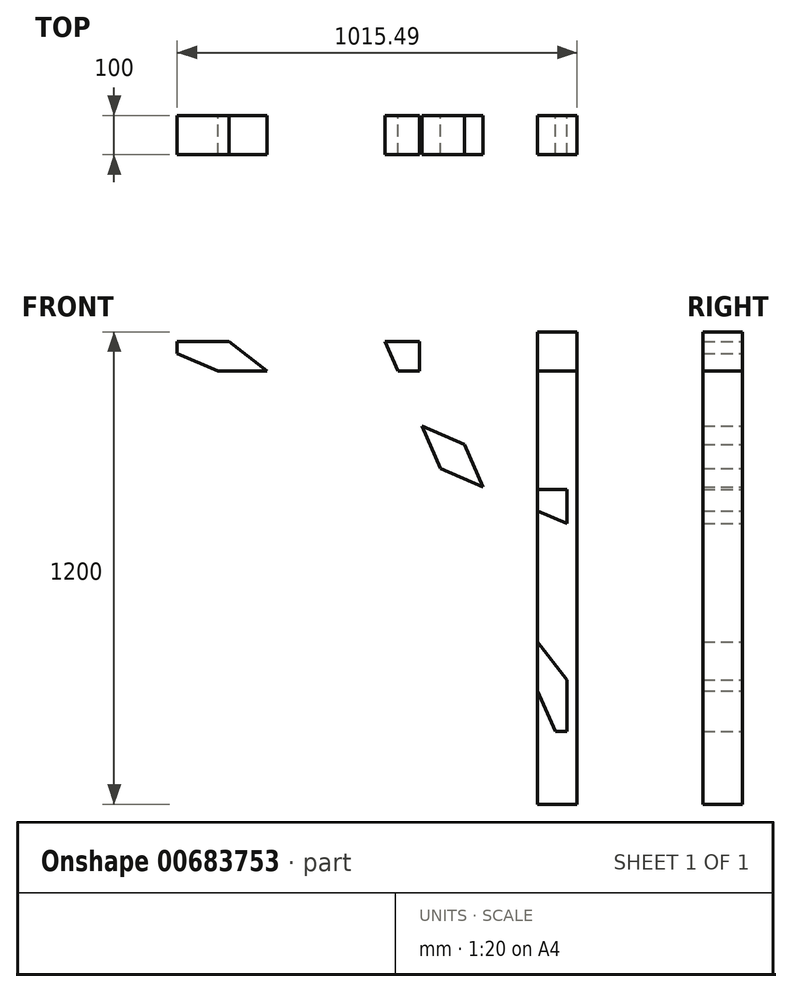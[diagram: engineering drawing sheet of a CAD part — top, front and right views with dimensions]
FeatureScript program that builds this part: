
annotation { "Feature Type Name" : "Feature", "Feature Type Description" : "" }
export const myFeature = defineFeature(function(context is Context, id is Id, definition is map)
    precondition{}
    {
        {
            var Q0;
            Q0=qCreatedBy(makeId("Front.planeOp"),FACE);
            var sketch = newSketch(context, id + "F0", { "sketchPlane" : qUnion([Q0])});
            skLineSegment(sketch, "E0.bottom", {"start": v(0, 1200) * mm, "end": v(1200, 1200) * mm});
            skLineSegment(sketch, "E0.top", {"start": v(0, 1100) * mm, "end": v(1200, 1100) * mm});
            skLineSegment(sketch, "E0.left", {"start": v(0, 1200) * mm, "end": v(0, 1100) * mm});
            skLineSegment(sketch, "E0.right", {"start": v(1200, 1200) * mm, "end": v(1200, 1100) * mm});
            skLineSegment(sketch, "E1.bottom", {"start": v(1200, 1200) * mm, "end": v(1100, 1200) * mm});
            skLineSegment(sketch, "E1.top", {"start": v(1200, 0) * mm, "end": v(1100, 0) * mm});
            skLineSegment(sketch, "E1.left", {"start": v(1200, 1200) * mm, "end": v(1200, 0) * mm});
            skLineSegment(sketch, "E1.right", {"start": v(1100, 1200) * mm, "end": v(1100, 0) * mm});
            skLineSegment(sketch, "E2", {"start": v(1200, 1200) * mm, "end": v(0, 0) * mm, "construction": true});
            skLineSegment(sketch, "E3", {"start": v(0, 1175) * mm, "end": v(1200, 1175) * mm, "construction": true});
            skLineSegment(sketch, "E4", {"start": v(1175, 1200) * mm, "end": v(1175, 0) * mm, "construction": true});
            skLineSegment(sketch, "E5", {"start": v(1145, 1200) * mm, "end": v(1145, 0) * mm, "construction": true});
            skLineSegment(sketch, "E6", {"start": v(0, 1145) * mm, "end": v(1200, 1145) * mm, "construction": true});
            skLineSegment(sketch, "E7", {"start": v(712.71, 1175) * mm, "end": v(1145, 184.5) * mm});
            skLineSegment(sketch, "E8", {"start": v(1145, 184.5) * mm, "end": v(1175, 184.5) * mm});
            skLineSegment(sketch, "E9", {"start": v(1175, 184.5) * mm, "end": v(1175, 315.77) * mm});
            skLineSegment(sketch, "E10", {"start": v(1175, 315.77) * mm, "end": v(1100, 412.61) * mm});
            skLineSegment(sketch, "E11", {"start": v(1100, 412.61) * mm, "end": v(1100, 487.61) * mm});
            skLineSegment(sketch, "E12", {"start": v(1100, 487.61) * mm, "end": v(832.73, 1100) * mm});
            skLineSegment(sketch, "E13", {"start": v(832.73, 1100) * mm, "end": v(800, 1100) * mm});
            skLineSegment(sketch, "E14", {"start": v(800, 1100) * mm, "end": v(800, 1175) * mm});
            skLineSegment(sketch, "E15", {"start": v(800, 1175) * mm, "end": v(712.71, 1175) * mm});
            skLineSegment(sketch, "E16", {"start": v(1175, 712.71) * mm, "end": v(184.5, 1145) * mm});
            skLineSegment(sketch, "E17", {"start": v(184.5, 1145) * mm, "end": v(184.5, 1175) * mm});
            skLineSegment(sketch, "E18", {"start": v(184.5, 1175) * mm, "end": v(315.77, 1175) * mm});
            skLineSegment(sketch, "E19", {"start": v(315.77, 1175) * mm, "end": v(412.61, 1100) * mm});
            skLineSegment(sketch, "E20", {"start": v(412.61, 1100) * mm, "end": v(487.61, 1100) * mm});
            skLineSegment(sketch, "E21", {"start": v(487.61, 1100) * mm, "end": v(1100, 832.73) * mm});
            skPoint(sketch, "E22", {"position": v(913.94, 913.94) * mm});
            skLineSegment(sketch, "E23", {"start": v(1100, 832.73) * mm, "end": v(1100, 800) * mm});
            skLineSegment(sketch, "E24", {"start": v(1100, 800) * mm, "end": v(1175, 800) * mm});
            skLineSegment(sketch, "E25", {"start": v(1175, 800) * mm, "end": v(1175, 712.71) * mm});
            skSolve(sketch);
        }
        {
            var Q0;
            {var subQ0=sQuery(id+"F0.wireOp",EDGE,"E14");Q0=makeQuery(id+"F0.imprint","IMPRINT",FACE,{"disambiguationData":[TD([[makeQuery(id+"F0.imprint","IMPRINT",EDGE,{"derivedFrom":subQ0}),1.0]])]});}
            var Q1;
            {var subQ0=sQuery(id+"F0.wireOp",EDGE,"E13");Q1=makeQuery(id+"F0.imprint","IMPRINT",FACE,{"disambiguationData":[TD([[makeQuery(id+"F0.imprint","IMPRINT",EDGE,{"derivedFrom":subQ0}),1.0]])]});}
            var Q2;
            {var subQ0=sQuery(id+"F0.wireOp",EDGE,"E16");var subQ1=sQuery(id+"F0.wireOp",EDGE,"E7");var subQ2=makeQuery(id+"F0.imprint","INTERSECT",VERTEX,{"derivedFrom":[subQ1,subQ0]});Q2=makeQuery(id+"F0.imprint","IMPRINT",FACE,{"disambiguationData":[TD([[makeQuery(id+"F0.imprint","IMPRINT",EDGE,{"disambiguationData":[TD([[subQ2,1.0]])],"derivedFrom":subQ1}),1.0]])]});}
            var Q3;
            {var subQ1=sQuery(id+"F0.wireOp",EDGE,"E11");Q3=makeQuery(id+"F0.imprint","IMPRINT",FACE,{"disambiguationData":[TD([[makeQuery(id+"F0.imprint","IMPRINT",EDGE,{"derivedFrom":subQ1}),1.0]])]});}
            var Q4;
            {var subQ0=sQuery(id+"F0.wireOp",EDGE,"E8");Q4=makeQuery(id+"F0.imprint","IMPRINT",FACE,{"disambiguationData":[TD([[makeQuery(id+"F0.imprint","IMPRINT",EDGE,{"derivedFrom":subQ0}),1.0]])]});}
            extrude(context, id + "F1", {"entities" : qUnion([Q0, Q1, Q2, Q3, Q4]), "depth" : 100 * mm, "offsetDistance" : 25 * mm});
        }
        {
            var Q0;
            {var subQ0=sQuery(id+"F0.wireOp",EDGE,"E17");Q0=makeQuery(id+"F0.imprint","IMPRINT",FACE,{"disambiguationData":[TD([[makeQuery(id+"F0.imprint","IMPRINT",EDGE,{"derivedFrom":subQ0}),-1.0]])]});}
            var Q1;
            {var subQ0=sQuery(id+"F0.wireOp",EDGE,"E20");Q1=makeQuery(id+"F0.imprint","IMPRINT",FACE,{"disambiguationData":[TD([[makeQuery(id+"F0.imprint","IMPRINT",EDGE,{"derivedFrom":subQ0}),-1.0]])]});}
            var Q2;
            {var subQ0=sQuery(id+"F0.wireOp",EDGE,"E16");var subQ1=sQuery(id+"F0.wireOp",EDGE,"E7");var subQ2=makeQuery(id+"F0.imprint","INTERSECT",VERTEX,{"derivedFrom":[subQ1,subQ0]});Q2=makeQuery(id+"F0.imprint","IMPRINT",FACE,{"disambiguationData":[TD([[makeQuery(id+"F0.imprint","IMPRINT",EDGE,{"disambiguationData":[TD([[subQ2,1.0]])],"derivedFrom":subQ1}),1.0]])]});}
            var Q3;
            {var subQ5=sQuery(id+"F0.wireOp",EDGE,"E23");Q3=makeQuery(id+"F0.imprint","IMPRINT",FACE,{"disambiguationData":[TD([[makeQuery(id+"F0.imprint","IMPRINT",EDGE,{"derivedFrom":subQ5}),-1.0]])]});}
            var Q4;
            {var subQ0=sQuery(id+"F0.wireOp",EDGE,"E24");Q4=makeQuery(id+"F0.imprint","IMPRINT",FACE,{"disambiguationData":[TD([[makeQuery(id+"F0.imprint","IMPRINT",EDGE,{"derivedFrom":subQ0}),-1.0]])]});}
            extrude(context, id + "F2", {"entities" : qUnion([Q0, Q1, Q2, Q3, Q4]), "depth" : 100 * mm, "offsetDistance" : 25 * mm});
        }
        {
            var Q0;
            {var subQ7=sQuery(id+"F0.wireOp",EDGE,"E0.bottom");Q0=makeQuery(id+"F0.imprint","IMPRINT",FACE,{"disambiguationData":[TD([[makeQuery(id+"F0.imprint","IMPRINT",EDGE,{"derivedFrom":subQ7}),-1.0]])]});}
            var Q1;
            {var subQ5=sQuery(id+"F0.wireOp",EDGE,"E1.bottom");Q1=makeQuery(id+"F0.imprint","IMPRINT",FACE,{"disambiguationData":[TD([[makeQuery(id+"F0.imprint","IMPRINT",EDGE,{"derivedFrom":subQ5}),1.0]])]});}
            extrude(context, id + "F3", {"entities" : qUnion([Q0, Q1]), "depth" : 100 * mm, "offsetDistance" : 25 * mm});
        }
        {
            var Q0;
            {var subQ5=sQuery(id+"F0.wireOp",EDGE,"E1.top");Q0=makeQuery(id+"F0.imprint","IMPRINT",FACE,{"disambiguationData":[TD([[makeQuery(id+"F0.imprint","IMPRINT",EDGE,{"derivedFrom":subQ5}),-1.0]])]});}
            extrude(context, id + "F4", {"entities" : qUnion([Q0]), "depth" : 100 * mm, "offsetDistance" : 25 * mm});
        }
    });
